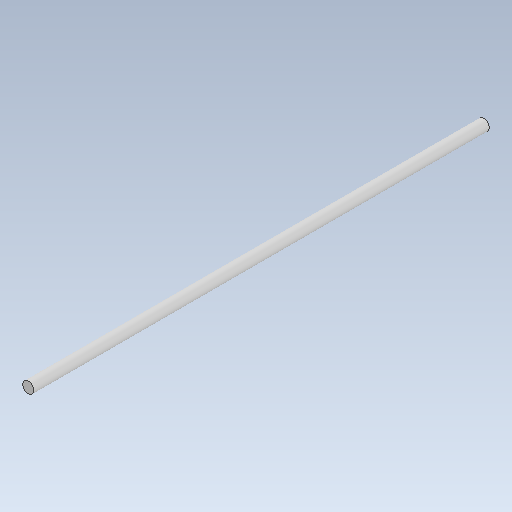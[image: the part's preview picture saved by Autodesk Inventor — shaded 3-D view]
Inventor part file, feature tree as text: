
AUTODESK INVENTOR PART (.ipt)
format: ipt  version: 2020 (Build 240168000, 168)  size: 82,432 bytes
history: native  units: in
note: dims shown in document units (in); Inventor stores cm internally (conversion verified against a paired STEP export)
features: extrude x1
ambient origin geometry x8: Origin, YZ Plane, XZ Plane, XY Plane, X Axis, Y Axis, Z Axis, Center Point
bodies: Solid1 (feature_tree)
feature tree (1):
  extrude  "Extrude1"  [1 undecoded]
note: 1 required parameter value undecoded (feature->parameter linkage not recoverable at this tier; creation-order binding heuristic only, values carry confidence <= 0.55)
